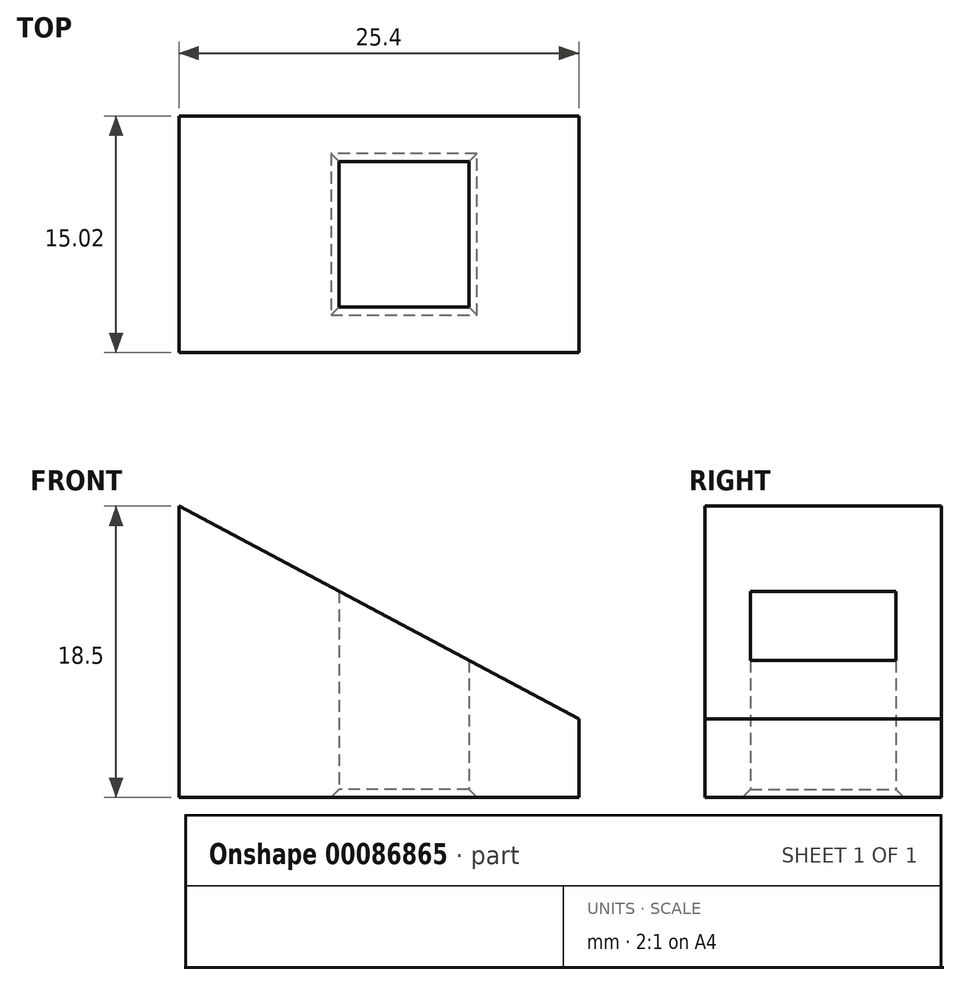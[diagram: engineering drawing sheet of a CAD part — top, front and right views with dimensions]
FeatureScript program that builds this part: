
annotation { "Feature Type Name" : "Feature", "Feature Type Description" : "" }
export const myFeature = defineFeature(function(context is Context, id is Id, definition is map)
    precondition{}
    {
        {
            var Q0;
            Q0=qCreatedBy(makeId("Top.planeOp"),FACE);
            var sketch = newSketch(context, id + "F0", { "sketchPlane" : qUnion([Q0])});
            skLineSegment(sketch, "E0.bottom", {"start": v(-12.7, 7.5) * mm, "end": v(12.7, 7.5) * mm});
            skLineSegment(sketch, "E0.top", {"start": v(-12.7, -7.5) * mm, "end": v(12.7, -7.5) * mm});
            skLineSegment(sketch, "E0.left", {"start": v(-12.7, 7.5) * mm, "end": v(-12.7, -7.5) * mm});
            skLineSegment(sketch, "E0.right", {"start": v(12.7, 7.5) * mm, "end": v(12.7, -7.5) * mm});
            skPoint(sketch, "E0.middle", {"position": v(0, 0) * mm});
            skLineSegment(sketch, "E1.bottom", {"start": v(-2.54, -4.62) * mm, "end": v(5.7, -4.62) * mm});
            skLineSegment(sketch, "E1.top", {"start": v(-2.54, 4.63) * mm, "end": v(5.7, 4.63) * mm});
            skLineSegment(sketch, "E1.left", {"start": v(-2.54, -4.62) * mm, "end": v(-2.54, 4.63) * mm});
            skLineSegment(sketch, "E1.right", {"start": v(5.7, -4.62) * mm, "end": v(5.7, 4.62) * mm});
            skPoint(sketch, "E1.middle", {"position": v(1.58, 0) * mm});
            skSolve(sketch);
        }
        {
            var Q0;
            Q0=makeQuery(id+"F0.imprint","IMPRINT",FACE,{"disambiguationData":[TD([[makeQuery(id+"F0.imprint","IMPRINT",EDGE,{"derivedFrom":sQuery(id+"F0.wireOp",EDGE,"E0.bottom")}),-1.0]])]});
            extrude(context, id + "F1", {"entities" : qUnion([Q0]), "depth" : 18.5 * mm});
        }
        {
            var Q0;
            Q0=makeQuery(id+"F1.opExtrude","SWEPT_FACE",FACE,{"disambiguationData":[OSD([sQuery(id+"F0.wireOp",EDGE,"E0.top")])]});
            var sketch = newSketch(context, id + "F2", { "sketchPlane" : qUnion([Q0])});
            skLineSegment(sketch, "E2", {"start": v(-12.7, 18.5) * mm, "end": v(12.7, 4.97) * mm});
            skLineSegment(sketch, "E3", {"start": v(12.7, 4.97) * mm, "end": v(12.7, 18.5) * mm});
            skLineSegment(sketch, "E4", {"start": v(12.7, 18.5) * mm, "end": v(-12.7, 18.5) * mm});
            skSolve(sketch);
        }
        {
            var Q0;
            Q0 = qSketchRegion(id + "F2", true);
            extrude(context, id + "F3", {"entities" : qUnion([Q0]), "operationType" : NewBodyOperationType.REMOVE, "oppositeDirection" : true, "depth" : 25.4 * mm});
        }
        {
            var Q0;
            Q0=makeQuery(id+"F1.opExtrude","CAP_EDGE",EDGE,{"disambiguationData":[OSD([sQuery(id+"F0.wireOp",EDGE,"E1.left")])],"isStart":true});
            var Q1;
            Q1=makeQuery(id+"F1.opExtrude","CAP_EDGE",EDGE,{"disambiguationData":[OSD([sQuery(id+"F0.wireOp",EDGE,"E1.top")])],"isStart":true});
            var Q2;
            Q2=makeQuery(id+"F1.opExtrude","CAP_EDGE",EDGE,{"disambiguationData":[OSD([sQuery(id+"F0.wireOp",EDGE,"E1.right")])],"isStart":true});
            var Q3;
            Q3=makeQuery(id+"F1.opExtrude","CAP_EDGE",EDGE,{"disambiguationData":[OSD([sQuery(id+"F0.wireOp",EDGE,"E1.bottom")])],"isStart":true});
            chamfer(context, id + "F4", {"entities" : qUnion([Q0, Q1, Q2, Q3]), "width" : 0.5 * mm, "tangentPropagation" : true});
        }
    });
